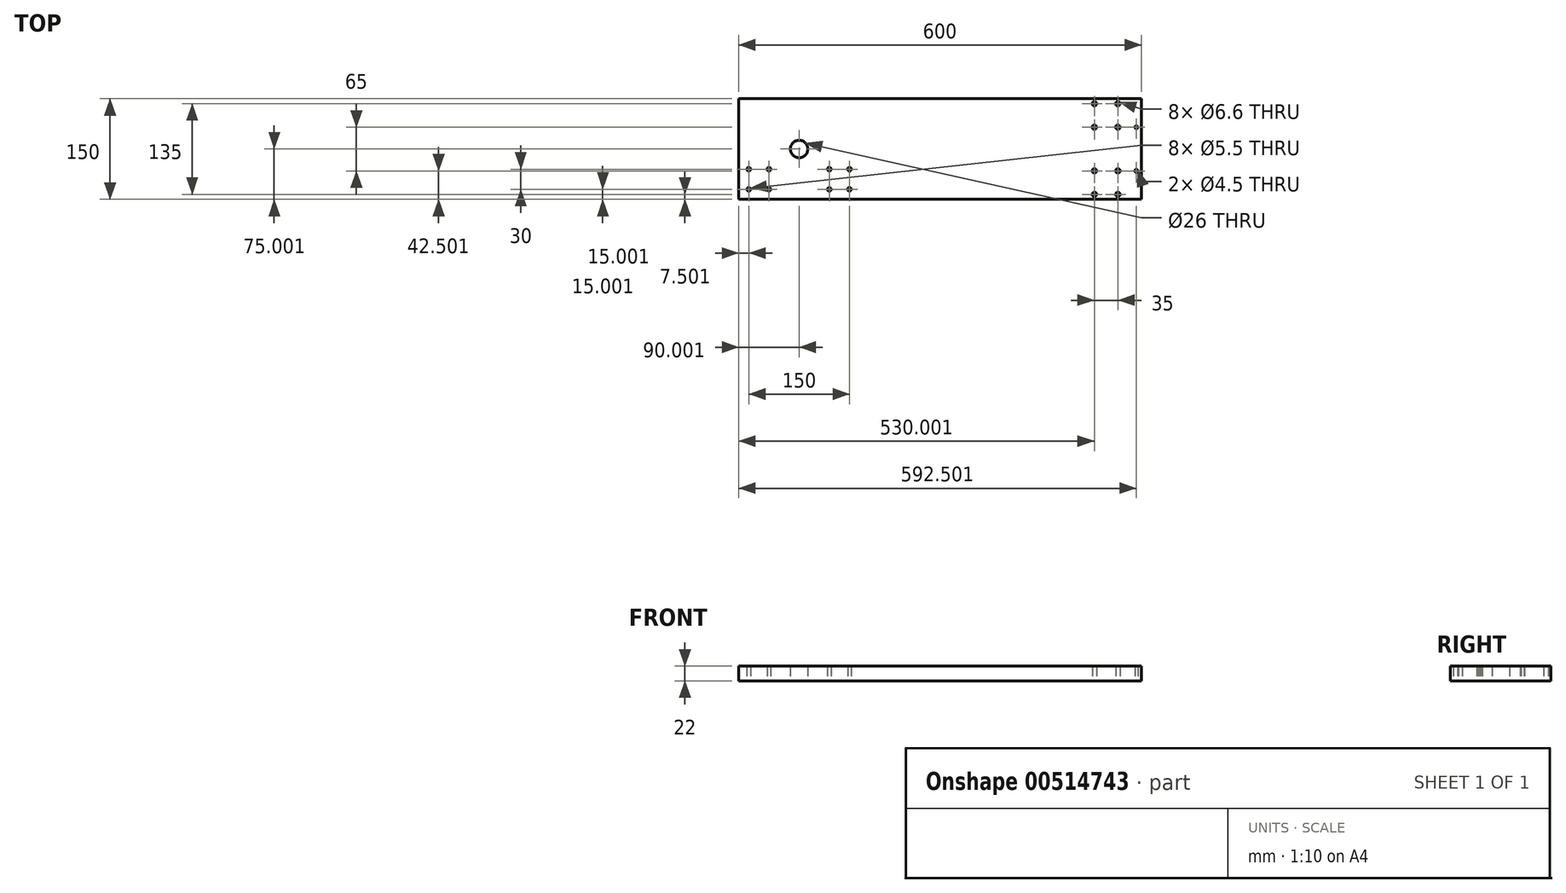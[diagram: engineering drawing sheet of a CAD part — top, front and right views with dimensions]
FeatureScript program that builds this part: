
annotation { "Feature Type Name" : "Feature", "Feature Type Description" : "" }
export const myFeature = defineFeature(function(context is Context, id is Id, definition is map)
    precondition{}
    {
        {
            var Q0;
            Q0=qCreatedBy(makeId("Top.planeOp"),FACE);
            var sketch = newSketch(context, id + "F0", { "sketchPlane" : qUnion([Q0])});
            skLineSegment(sketch, "E0", {"start": v(-30.95, 156.47) * mm, "end": v(569.05, 156.47) * mm});
            skLineSegment(sketch, "E1", {"start": v(569.05, 156.47) * mm, "end": v(569.05, 6.47) * mm});
            skLineSegment(sketch, "E2", {"start": v(569.05, 6.47) * mm, "end": v(-30.95, 6.47) * mm});
            skLineSegment(sketch, "E3", {"start": v(-30.95, 6.47) * mm, "end": v(-30.95, 156.47) * mm});
            skPoint(sketch, "E4", {"position": v(534.05, 13.97) * mm});
            skPoint(sketch, "E5", {"position": v(499.05, 13.97) * mm});
            skPoint(sketch, "E6", {"position": v(499.05, 48.97) * mm});
            skPoint(sketch, "E7", {"position": v(534.05, 48.97) * mm});
            skPoint(sketch, "E8", {"position": v(534.05, 113.97) * mm});
            skPoint(sketch, "E9", {"position": v(499.05, 113.97) * mm});
            skPoint(sketch, "E10", {"position": v(499.05, 148.97) * mm});
            skPoint(sketch, "E11", {"position": v(534.05, 148.97) * mm});
            skPoint(sketch, "E12", {"position": v(561.55, 113.97) * mm});
            skPoint(sketch, "E13", {"position": v(561.55, 48.97) * mm});
            skPoint(sketch, "E14", {"position": v(-15.95, 21.47) * mm});
            skPoint(sketch, "E15", {"position": v(14.05, 21.47) * mm});
            skPoint(sketch, "E16", {"position": v(14.05, 51.47) * mm});
            skPoint(sketch, "E17", {"position": v(-15.95, 51.47) * mm});
            skPoint(sketch, "E18", {"position": v(104.05, 21.47) * mm});
            skPoint(sketch, "E19", {"position": v(134.05, 21.47) * mm});
            skPoint(sketch, "E20", {"position": v(134.05, 51.47) * mm});
            skPoint(sketch, "E21", {"position": v(104.05, 51.47) * mm});
            skPoint(sketch, "E22", {"position": v(59.05, 81.47) * mm});
            skSolve(sketch);
        }
        {
            var Q0;
            Q0=makeQuery(id+"F0.imprint","IMPRINT",FACE,{"disambiguationData":[TD([[makeQuery(id+"F0.imprint","IMPRINT",EDGE,{"derivedFrom":sQuery(id+"F0.wireOp",EDGE,"E0")}),-1.0]])]});
            extrude(context, id + "F1", {"entities" : qUnion([Q0]), "depth" : 22 * mm, "offsetDistance" : 25 * mm});
        }
        {
            var Q0;
            Q0=sQuery(id+"F0.wireOp",VERTEX,"E9");
            var Q1;
            Q1=sQuery(id+"F0.wireOp",VERTEX,"E8");
            var Q2;
            Q2=sQuery(id+"F0.wireOp",VERTEX,"E10");
            var Q3;
            Q3=sQuery(id+"F0.wireOp",VERTEX,"E11");
            var Q4;
            Q4=sQuery(id+"F0.wireOp",VERTEX,"E4");
            var Q5;
            Q5=sQuery(id+"F0.wireOp",VERTEX,"E6");
            var Q6;
            Q6=sQuery(id+"F0.wireOp",VERTEX,"E5");
            var Q7;
            Q7=sQuery(id+"F0.wireOp",VERTEX,"E7");
            var Q8;
            Q8=makeQuery(id+"F1.opExtrude","SWEPT_BODY",BODY,{"disambiguationData":[OSD([sQuery(id+"F0.wireOp",EDGE,"E0"),sQuery(id+"F0.wireOp",EDGE,"E1"),sQuery(id+"F0.wireOp",EDGE,"E2"),sQuery(id+"F0.wireOp",EDGE,"E3")])]});
            hole(context, id + "F2", {"style" : HoleStyle.SIMPLE, "endStyle" : HoleEndStyle.THROUGH, "oppositeDirection" : true, "holeDiameter" : 6.6 * mm, "isTappedThrough" : true, "tappedDepth" : 12 * mm, "tapClearance" : 3, "locations" : qUnion([Q0, Q1, Q2, Q3, Q4, Q5, Q6, Q7]), "scope" : qUnion([Q8])});
        }
        {
            var Q0;
            Q0=sQuery(id+"F0.wireOp",VERTEX,"E14");
            var Q1;
            Q1=sQuery(id+"F0.wireOp",VERTEX,"E15");
            var Q2;
            Q2=sQuery(id+"F0.wireOp",VERTEX,"E21");
            var Q3;
            Q3=sQuery(id+"F0.wireOp",VERTEX,"E18");
            var Q4;
            Q4=sQuery(id+"F0.wireOp",VERTEX,"E16");
            var Q5;
            Q5=sQuery(id+"F0.wireOp",VERTEX,"E20");
            var Q6;
            Q6=sQuery(id+"F0.wireOp",VERTEX,"E19");
            var Q7;
            Q7=sQuery(id+"F0.wireOp",VERTEX,"E17");
            var Q8;
            Q8=makeQuery(id+"F1.opExtrude","SWEPT_BODY",BODY,{"disambiguationData":[OSD([sQuery(id+"F0.wireOp",EDGE,"E0"),sQuery(id+"F0.wireOp",EDGE,"E1"),sQuery(id+"F0.wireOp",EDGE,"E2"),sQuery(id+"F0.wireOp",EDGE,"E3")])]});
            hole(context, id + "F3", {"style" : HoleStyle.SIMPLE, "endStyle" : HoleEndStyle.THROUGH, "oppositeDirection" : true, "holeDiameter" : 5.5 * mm, "isTappedThrough" : true, "tappedDepth" : 12 * mm, "tapClearance" : 3, "locations" : qUnion([Q0, Q1, Q2, Q3, Q4, Q5, Q6, Q7]), "scope" : qUnion([Q8])});
        }
        {
            var Q0;
            Q0=sQuery(id+"F0.wireOp",VERTEX,"E22");
            var Q1;
            Q1=makeQuery(id+"F1.opExtrude","SWEPT_BODY",BODY,{"disambiguationData":[OSD([sQuery(id+"F0.wireOp",EDGE,"E0"),sQuery(id+"F0.wireOp",EDGE,"E1"),sQuery(id+"F0.wireOp",EDGE,"E2"),sQuery(id+"F0.wireOp",EDGE,"E3")])]});
            hole(context, id + "F4", {"style" : HoleStyle.SIMPLE, "endStyle" : HoleEndStyle.THROUGH, "oppositeDirection" : true, "holeDiameter" : 26 * mm, "isTappedThrough" : true, "tappedDepth" : 12 * mm, "tapClearance" : 3, "locations" : qUnion([Q0]), "scope" : qUnion([Q1])});
        }
        {
            var Q0;
            Q0=sQuery(id+"F0.wireOp",VERTEX,"E12");
            var Q1;
            Q1=sQuery(id+"F0.wireOp",VERTEX,"E13");
            var Q2;
            Q2=makeQuery(id+"F1.opExtrude","SWEPT_BODY",BODY,{"disambiguationData":[OSD([sQuery(id+"F0.wireOp",EDGE,"E0"),sQuery(id+"F0.wireOp",EDGE,"E1"),sQuery(id+"F0.wireOp",EDGE,"E2"),sQuery(id+"F0.wireOp",EDGE,"E3")])]});
            hole(context, id + "F5", {"style" : HoleStyle.SIMPLE, "endStyle" : HoleEndStyle.THROUGH, "oppositeDirection" : true, "holeDiameter" : 4.5 * mm, "isTappedThrough" : true, "tappedDepth" : 12 * mm, "tapClearance" : 3, "locations" : qUnion([Q0, Q1]), "scope" : qUnion([Q2])});
        }
    });
